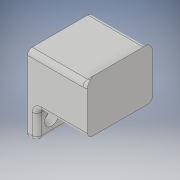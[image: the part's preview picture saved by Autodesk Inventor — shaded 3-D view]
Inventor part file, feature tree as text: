
AUTODESK INVENTOR PART (.ipt)
format: ipt  version: 2018 (Build 220112000, 112)  size: 358,400 bytes
history: native  units: in
note: dims shown in document units (in); Inventor stores cm internally (conversion verified against a paired STEP export)
features: reference x23, sketch x15, extrude x14, other x9, fillet x5, projected_geometry x3
ambient origin geometry x8: Origin, YZ Plane, XZ Plane, XY Plane, X Axis, Y Axis, Z Axis, Center Point
bodies: Solid1 (feature_tree)
feature tree (69):
  extrude  "Extrusion1"  Depth=0.125in
  extrude  "Extrusion2"  Depth=0.4724in TaperAngle=0.0deg
  sketch  "Sketch3"  dims[d5=0.0787in d6=0.0in d7=0.2in d8=0.0in]
  extrude  "Extrusion3"  Depth=0.0787in TaperAngle=0.0deg
  extrude  "Extrusion4"  Depth=0.4in
  extrude  "Extrusion5"  Depth=0.25in
  extrude  "Extrusion6"  Depth=0.0787in TaperAngle=0.0deg
  extrude  "Extrusion7"  Depth=0.1181in
  extrude  "Extrusion8"  Depth=0.1181in
  extrude  "Extrusion10"  Depth=0.0787in TaperAngle=0.0deg
  extrude  "Extrusion12"  Depth=0.25in TaperAngle=0.0deg
  fillet  "Fillet2"  Radius=0.75in
  fillet  "Fillet3"  Radius=0.75in
  extrude  "Extrusion13"  Depth=0.0394in
  fillet  "Fillet4"  Radius=1.0in
  fillet  "Fillet6"  Radius=0.0394in
  extrude  "Extrusion14"  Depth=0.0394in
  fillet  "Fillet8"  Radius=1.0in
  extrude  "Extrusion15"  Depth=0.0394in
  extrude  "Extrusion16"  Depth=0.0394in
  sketch  "Sketch1"  dims[d0=0.5in d1=0.125in]
  reference  "Reference1"
  reference  "Reference2"
  reference  "Reference3"
  reference  "Reference4"
  reference  "Reference5"
  reference  "Reference6"
  reference  "Reference7"
  reference  "Reference8"
  reference  "Reference9"
  reference  "Reference10"
  reference  "Reference11"
  reference  "Reference12"
  reference  "Reference13"
  reference  "Reference14"
  reference  "Reference15"
  reference  "Reference16"
  reference  "Reference17"
  sketch  "Sketch2"  dims[d2=0.7in d3=0.4724in d4=0.0in]
  projected_geometry  "Projected Loop1"
  projected_geometry  "Projected Loop2"
  reference  "Reference18"
  reference  "Reference19"
  sketch  "Sketch4"  dims[d9=0.4in d10=0.4in]
  projected_geometry  "Projected Loop3"
  sketch  "Sketch5"  dims[d11=0.5512in d12=0.0in d13=0.25in]
  reference  "Reference20"
  sketch  "Sketch6"  dims[d14=0.25in d15=0.0787in d16=0.0in]
  sketch  "Sketch7"  dims[d17=0.125in d18=0.1181in]
  sketch  "Sketch8"  dims[d19=0.125in d20=0.1181in]
  reference  "Reference21"
  sketch  "Sketch9"  dims[d21=1.15in d22=0.0787in d23=0.0in]
  sketch  "Sketch11"  dims[d24=1.0in d25=0.0in d26=0.25in d27=0.0in d31=0.75in d32=0.75in]
  reference  "Reference23"
  sketch  "Sketch13"  dims[d33=0.5in d34=0.0in d38=0.1575in d39=1.0in d40=0.0in d42=0.0394in]
  reference  "Reference25"
  sketch  "Sketch14"  dims[d43=0.0394in d44=0.65in d45=1.0in d46=0.0in]
  sketch  "Sketch15"  dims[d47=0.0394in d49=0.0394in]
  sketch  "Sketch16"  dims[d51=0.0098in d52=0.0in d53=0.0394in]
  sketch  "Sketch17"  dims[d54=1.0in d55=0.0in d56=1.0in d57=0.0in]
  other  "<userpath>\OneDrive\Documents\Inventor\TSA\2018\Animatronics\Tortoise\AssemblyTURTLE.iam"
  other  "AssemblyTURTLE.iam"
  other  "servo (2):1"
  other  "smallergear:1"
  other  "Frame:1"
  other  "<userpath>\OneDrive\Documents\Inventor\TSA\2018\Animatronics\Tortoise\TurtleAssembly.iam"
  other  "TurtleAssembly.iam"
  other  "smallergear:3"
  other  "holder_gear_mount:1"
